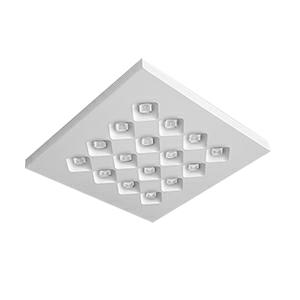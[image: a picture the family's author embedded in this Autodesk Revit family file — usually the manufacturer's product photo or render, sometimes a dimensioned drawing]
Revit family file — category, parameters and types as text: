
# Revit family: 3f_filippi_-_3f_diagon_3f_filippi_-_23126_a0686_-_3f_diagon_25w-940_dali_596x596___corn_plaf__e588
name_source: partatom
category: Lighting Fixtures
units: mm (PartAtom-declared; Revit-internal decimal feet)

## family parameters
Cut with Voids When Loaded = No
Host = Face
Light Source = No
Part Type = Normal
Room Calculation Point = No
Round Connector Dimension = Use Diameter
Shared = No

## types (1)
- 3F Filippi - 3F Dìagon (1 x LED, 3294 lm, 28 W, 4000 K)
    Apparent Load = 28 VA
    Approval mark = CE
    CIE Flux Codes = 67 96 100 100 100
    Color Rendering = 90
    Color Temperature = 4000 K
    Control Gear = Electronic transformer
    Default Elevation = 1800 mm
    Description = ILLUMINOTECHNICAL
Luminous efficiency 100% (DLOR 100%, ULOR 0%).
Initial luminous flux of the luminaire 3294 lm.
Direct symmetric distribution.
Installation Interdistance Transv.D = 1.39 x hu - Long.D = 1.39 x hu.
Average luminance <1500 cd/m² for radial angles >65°.
Tabular UGR (CIE 117 - 4H-8H; S=0.25H; 70/50/20): RUG 16.5 - 16.4.
Beam angle: 93° - 92°.
Luminous efficacy 118 lm/W.
Lifetime (L95/B10): 30000 h. (tq+25°C)
Lifetime (L90/B10): 50000 h. (tq+25°C)
Lifetime (L80/B10): 80000 h. (tq+25°C)
Lifetime (L75/B10): 100000 h. (tq+25°C)
Sudden decreased luminous flux after 50000 hours: 0% (C0).
Photobiological safety in compliance with IEC/TR 62778: RG0 risk exempt, (IEC 62471).
In compliance with IEC/EN 62722-2-1 - IEC/EN 62717 standards.

SOURCE
Squared LED module 25W/940.
Energy efficiency class (UE 2019/2020 - UE 2019/2015): D.
CIE 13.3 Colour rendering index: CRI >90 (R9 >50%).
IES TM-30 Fidelity Index: Rf = 92 Rg = 101.
CCT nominal colour temperature 4000 K.
Colour initial tolerance (MacAdam): SDCM 3.

MECHANICAL
Housing in hot-galvanised steel, painted in white polyester.
Honeycombed diagonal screen in white anti-glare polycarbonate.
Rhomboidal lenses with differentiated surfaces, etched and prismatic to optimise the orientation of the luminous flux, in transparent methacrylate (PMMA).
Luminaire with limited surface temperature. - D - (EN 60598-2-24)
Dimensions: 600x600 mm, height 40 mm. Weight 6.075 kg.
IP43 protection degree for exposed part, IP20 for recessed part.
Mechanical strength to impacts IK06 (1 joule).
Glow-wire test resistance 650°C.

ELECTRICAL
Halogen Free DALI-2, PUSH-DIM, electronic wiring 230V-50/60Hz, power factor 0.95 at full load, THD <25%, constant output current, class I, 1 driver, 1 DALI addresse.
Power of the luminaire 28 W.
ENEC - CE.
SAFE FLICKER: PstLM=<1 and SVM=<0.4 (IEC TR 61547-1 and IEC TR 63158), to ensure a more comfortable and safe light.
Luminaire compliant with EN 60598-2-22 for power supply from a centralised emergency system CPSS (Central Power Supply System), not incorporated in the luminaire - high risk areas excluded. The default power and flux are 100% in AC and 15% in DC.
Ambient temperature from 0°C to +25°C.
Temperature class T6 max 85°C.
Quick connection.
Relative humidity UR: <85%.

INSTALLATION
Ceiling.
Height only 40 mm.
All accessories dedicated to this product are available on the Catalog and on our website www.3F-Filippi.com.

ACCESSORIES
A0686 - 596x596 Diagon frame for Ceiling installation.

APPLICATIONS
Environments: staterooms, with VDTs, offices.
Environments with exacting visual tasks, where diffused soft light for optimum visual comfort is required.

LIGHT MANAGEMENT
Recommended minimum setting: 10%.
The device, equipped with DALI-2 driver, can be controlled manually with 3F Easy Dim technology or automatically/manually with 3F Smart Dimming technology and/or centralised DALI systems.
DALI-2 certification guarantees interoperability with other devices with the same certification.
In electrical systems without a regulation system (manual or automatic) and DALI bus, a suitable jumper must be made on the DA-DA terminals of the appliance.

WARNING
Luminaire designed for disposal/recycling at end-of-life.
Replaceable (LED only) light source by a professional. Replaceable control gear by a professional.
    Height = 0 mm  [stored 0 ft]
    Lamp = 1 x LED
    Lamp Light Flux = 3294 lm
    Lamp Power = 28 W
    Lamp count = 1
    Length = 600 mm
    Lifetime = 50000 h
    Luminous efficacy = 118 lm/W
    Manufacturer = 3F Filippi
    ModVariant = No
    Model = 3F Filippi - 23126+A0686 - 3F Diagon 25W-940 DALI 596x596 + Corn.plaf.
    Mounting Place = Ceiling
    Mounting Type = Recessed
    Number of Poles = 1
    OnlyDefault = Yes
    Power Factor = 1
    Product Name = 3F Filippi - 3F Dìagon
    Product group = recessed luminaire
    ProductGroupID = 4
    Protection Class = Protection class I
    Protection Degree = IP 20
    RLX_Detail_Level = 1
    RLX_Emergency_Light_Flux = 0 lm
    RLX_Emergency_Type = 0
    RLX_Emergency_Type_DB = No
    RlxData = <blob elided: 98125 chars, md5=b01cd39e>
    Socket = socket
    Standby Power = 0 W
    System Light Flux = 3294 lm
    System Power = 28 W
    Type Comments = Product without accessories
    Type Image = 3ffilippi_3f_diagon__a0686.jpg
    URL = http://relux.com
    VarID = ---
    Voltage = 0 V
    Weight = 0.00 kg
    Width = 600 mm

note: [stored X ft] marks values corroborated as IEEE doubles in the binary element streams (Revit-internal decimal feet)

## geometry (parser evidence)
native form markers: Blend x4, Sweep x9
no freeform markers — native parametric forms only
